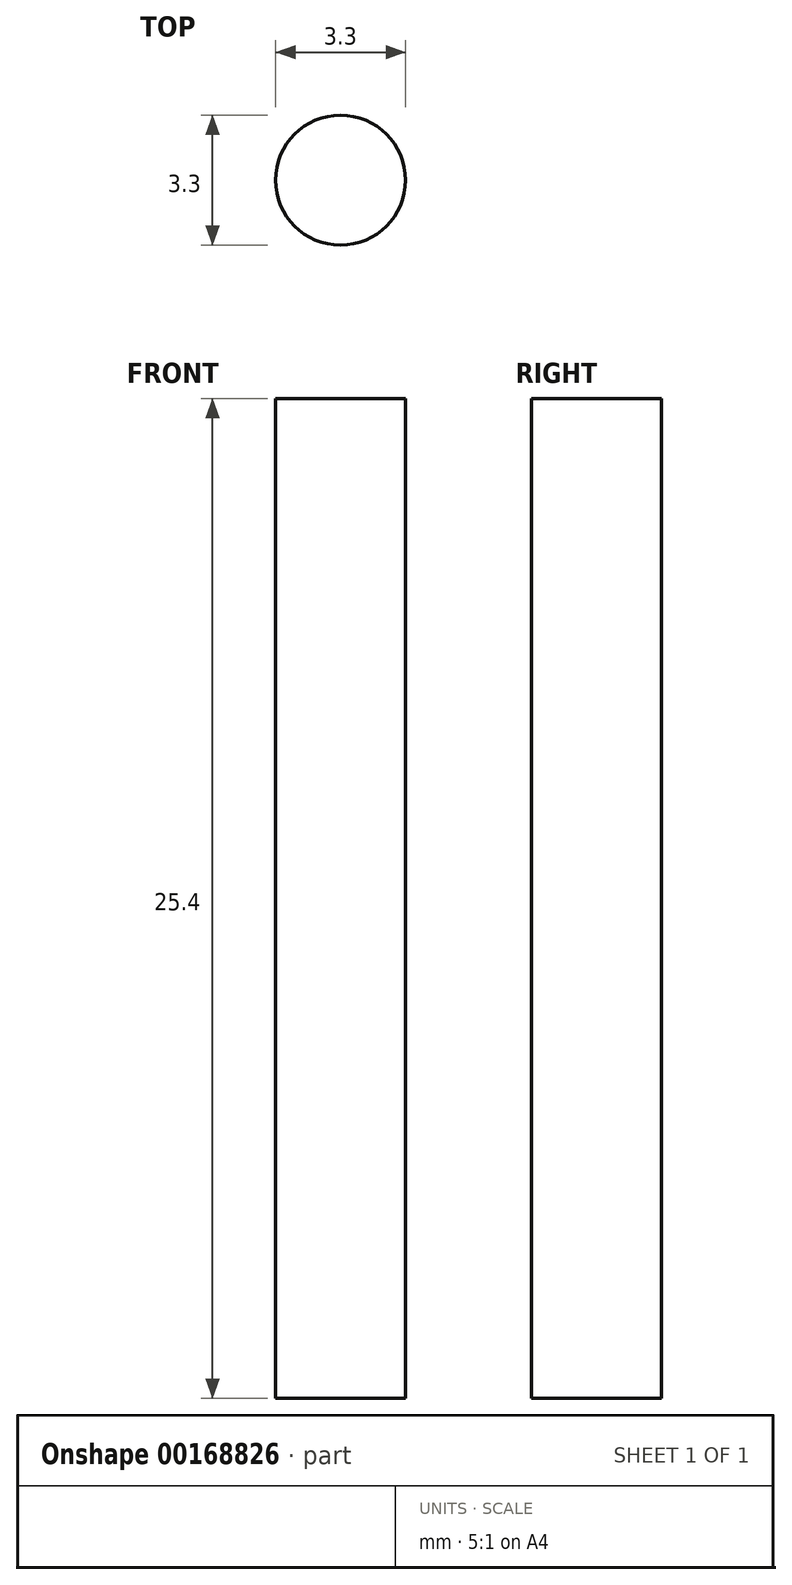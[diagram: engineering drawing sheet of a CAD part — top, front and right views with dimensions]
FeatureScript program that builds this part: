
annotation { "Feature Type Name" : "Feature", "Feature Type Description" : "" }
export const myFeature = defineFeature(function(context is Context, id is Id, definition is map)
    precondition{}
    {
        {
            var Q0;
            Q0=qCreatedBy(makeId("Top.planeOp"),FACE);
            var sketch = newSketch(context, id + "F0", { "sketchPlane" : qUnion([Q0])});
            skCircle(sketch, "E0", {"center": v(0, 0) * mm, "radius": 1.65 * mm});
            skSolve(sketch);
        }
        {
            var Q0;
            Q0 = qSketchRegion(id + "F0", true);
            extrude(context, id + "F1", {"entities" : qUnion([Q0]), "depth" : 25.4 * mm});
        }
    });
